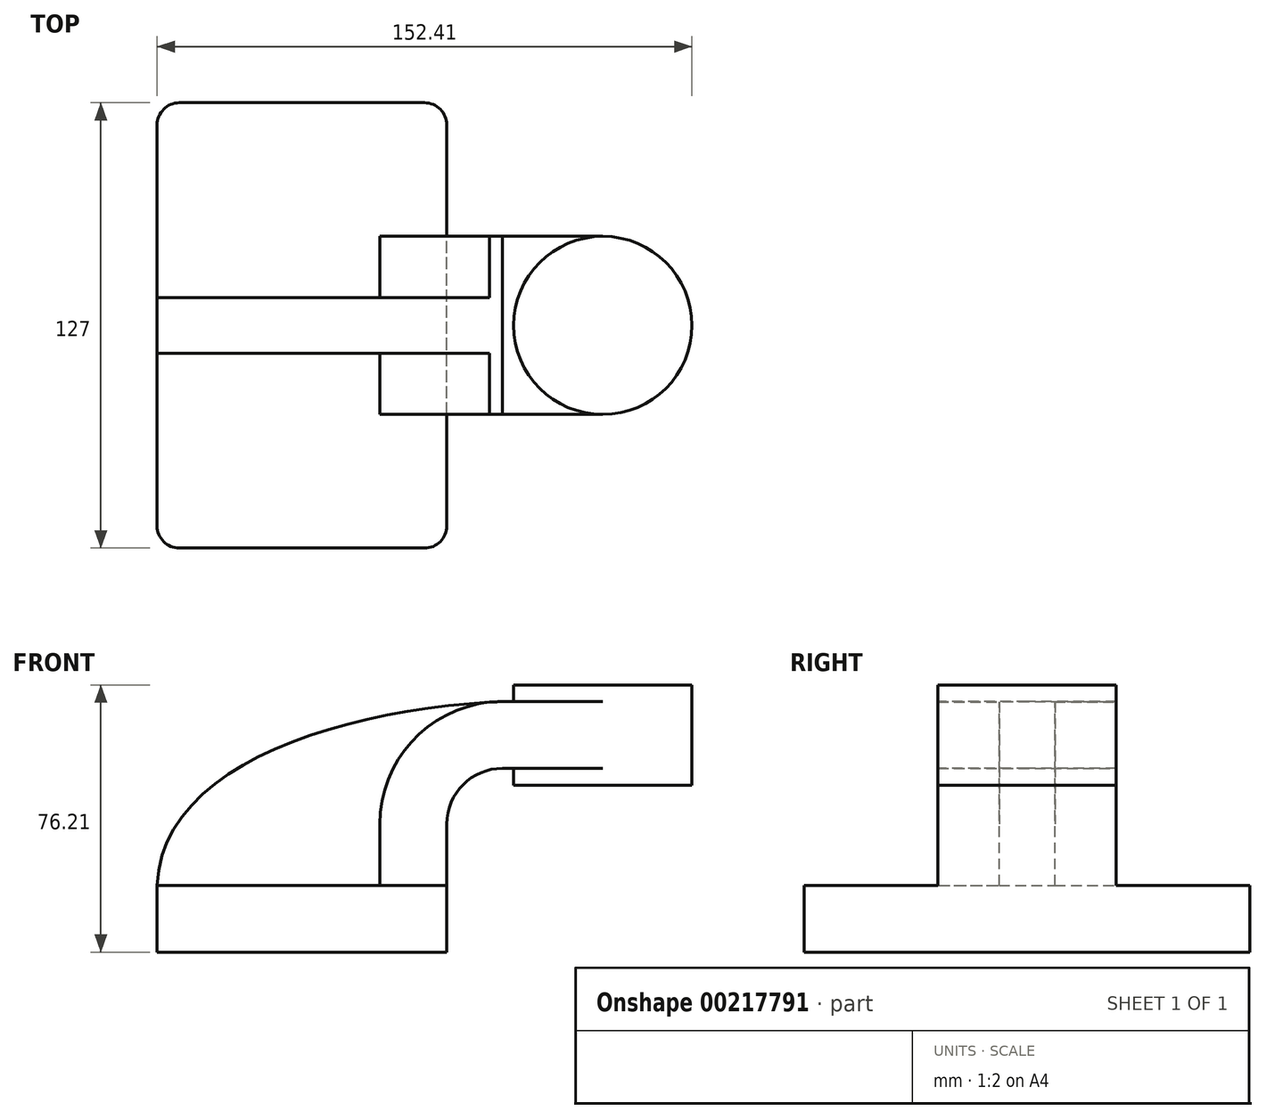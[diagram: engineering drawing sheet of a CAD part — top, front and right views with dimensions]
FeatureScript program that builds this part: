
annotation { "Feature Type Name" : "Feature", "Feature Type Description" : "" }
export const myFeature = defineFeature(function(context is Context, id is Id, definition is map)
    precondition{}
    {
        {
            var Q0;
            Q0=qCreatedBy(makeId("Front.planeOp"),FACE);
            var sketch = newSketch(context, id + "F0", { "sketchPlane" : qUnion([Q0])});
            skLineSegment(sketch, "E0.bottom", {"start": v(-41.27, -9.53) * mm, "end": v(41.28, -9.53) * mm});
            skLineSegment(sketch, "E0.top", {"start": v(-41.28, 9.52) * mm, "end": v(41.28, 9.52) * mm});
            skLineSegment(sketch, "E0.left", {"start": v(-41.27, -9.53) * mm, "end": v(-41.28, 9.52) * mm});
            skLineSegment(sketch, "E0.right", {"start": v(41.28, -9.53) * mm, "end": v(41.28, 9.52) * mm});
            skPoint(sketch, "E0.middle", {"position": v(0, 0) * mm});
            skLineSegment(sketch, "E1.bottom", {"start": v(60.33, 38.1) * mm, "end": v(111.12, 38.1) * mm});
            skLineSegment(sketch, "E1.top", {"start": v(60.33, 66.67) * mm, "end": v(111.12, 66.67) * mm});
            skLineSegment(sketch, "E1.left", {"start": v(60.33, 38.1) * mm, "end": v(60.33, 66.67) * mm});
            skLineSegment(sketch, "E1.right", {"start": v(111.12, 38.1) * mm, "end": v(111.12, 66.67) * mm});
            skPoint(sketch, "E1.middle", {"position": v(85.72, 52.39) * mm});
            skLineSegment(sketch, "E2", {"start": v(41.27, 9.52) * mm, "end": v(41.27, 27) * mm});
            skArc(sketch, "E3", {"start": v(41.27, 27) * mm, "mid": v(45.92, 38.23) * mm, "end": v(57.15, 42.88) * mm});
            skLineSegment(sketch, "E4", {"start": v(57.15, 42.88) * mm, "end": v(95.99, 42.88) * mm});
            skLineSegment(sketch, "E5.0", {"start": v(57.15, 61.93) * mm, "end": v(95.99, 61.93) * mm});
            skArc(sketch, "E5.1", {"start": v(22.23, 27) * mm, "mid": v(32.45, 51.7) * mm, "end": v(57.15, 61.93) * mm});
            skLineSegment(sketch, "E5.2", {"start": v(22.22, 9.52) * mm, "end": v(22.22, 27) * mm});
            skLineSegment(sketch, "E6", {"start": v(85.72, 38.1) * mm, "end": v(85.72, 66.67) * mm});
            skFitSpline(sketch, "E7", {"points": [v(-41.28, 9.52) * mm, v(57.15, 61.93) * mm], "startDerivative": vector(3.97, 104.04) * mm, "endDerivative": vector(136.46, 6.1) * mm});
            skSolve(sketch);
        }
        {
            var Q0;
            Q0=makeQuery(id+"F0.imprint","IMPRINT",FACE,{"disambiguationData":[TD([[makeQuery(id+"F0.imprint","IMPRINT",EDGE,{"derivedFrom":sQuery(id+"F0.wireOp",EDGE,"E0.bottom")}),1.0]])]});
            extrude(context, id + "F1", {"entities" : qUnion([Q0]), "endBound" : BoundingType.SYMMETRIC, "depth" : 127 * mm});
        }
        {
            var Q0;
            {var subQ1=sQuery(id+"F0.wireOp",EDGE,"E2");Q0=makeQuery(id+"F0.imprint","IMPRINT",FACE,{"disambiguationData":[TD([[makeQuery(id+"F0.imprint","IMPRINT",EDGE,{"derivedFrom":subQ1}),1.0]])]});}
            var Q1;
            {var subQ0=sQuery(id+"F0.wireOp",EDGE,"E4");var subQ1=sQuery(id+"F0.wireOp",EDGE,"E1.left");var subQ2=makeQuery(id+"F0.imprint","INTERSECT",VERTEX,{"derivedFrom":[subQ1,subQ0]});Q1=makeQuery(id+"F0.imprint","IMPRINT",FACE,{"disambiguationData":[TD([[makeQuery(id+"F0.imprint","IMPRINT",EDGE,{"disambiguationData":[TD([[subQ2,-1.0]])],"derivedFrom":subQ1}),-1.0]])]});}
            extrude(context, id + "F2", {"entities" : qUnion([Q0, Q1]), "operationType" : NewBodyOperationType.ADD, "endBound" : BoundingType.SYMMETRIC, "depth" : 50.8 * mm});
        }
        {
            var Q0;
            {var subQ3=sQuery(id+"F0.wireOp",EDGE,"E5.2");Q0=makeQuery(id+"F0.imprint","IMPRINT",FACE,{"disambiguationData":[TD([[makeQuery(id+"F0.imprint","IMPRINT",EDGE,{"derivedFrom":subQ3}),1.0]])]});}
            extrude(context, id + "F3", {"entities" : qUnion([Q0]), "operationType" : NewBodyOperationType.ADD, "endBound" : BoundingType.SYMMETRIC, "depth" : 15.88 * mm});
        }
        {
            var Q0;
            {var subQ0=sQuery(id+"F0.wireOp",EDGE,"E1.right");Q0=makeQuery(id+"F0.imprint","IMPRINT",FACE,{"disambiguationData":[TD([[makeQuery(id+"F0.imprint","IMPRINT",EDGE,{"derivedFrom":subQ0}),1.0]])]});}
            var Q1;
            Q1=sQuery(id+"F0.wireOp",EDGE,"E6");
            revolve(context, id + "F4", {"operationType" : NewBodyOperationType.ADD, "entities" : qUnion([Q0]), "axis" : qUnion([Q1]), "revolveType" : RevolveType.FULL});
        }
        {
            var Q0;
            Q0=makeQuery(id+"F1.opExtrude","CAP_EDGE",EDGE,{"disambiguationData":[OSD([sQuery(id+"F0.wireOp",EDGE,"E0.right")])],"isStart":true});
            var Q1;
            Q1=makeQuery(id+"F1.opExtrude","CAP_EDGE",EDGE,{"disambiguationData":[OSD([sQuery(id+"F0.wireOp",EDGE,"E0.right")])],"isStart":false});
            var Q2;
            Q2=makeQuery(id+"F1.opExtrude","CAP_EDGE",EDGE,{"disambiguationData":[OSD([sQuery(id+"F0.wireOp",EDGE,"E0.left")])],"isStart":false});
            var Q3;
            Q3=makeQuery(id+"F1.opExtrude","CAP_EDGE",EDGE,{"disambiguationData":[OSD([sQuery(id+"F0.wireOp",EDGE,"E0.left")])],"isStart":true});
            fillet(context, id + "F5", {"entities" : qUnion([Q0, Q1, Q2, Q3]), "radius" : 6.35 * mm, "tangentPropagation" : true, "allowEdgeOverflow" : false});
        }
    });
